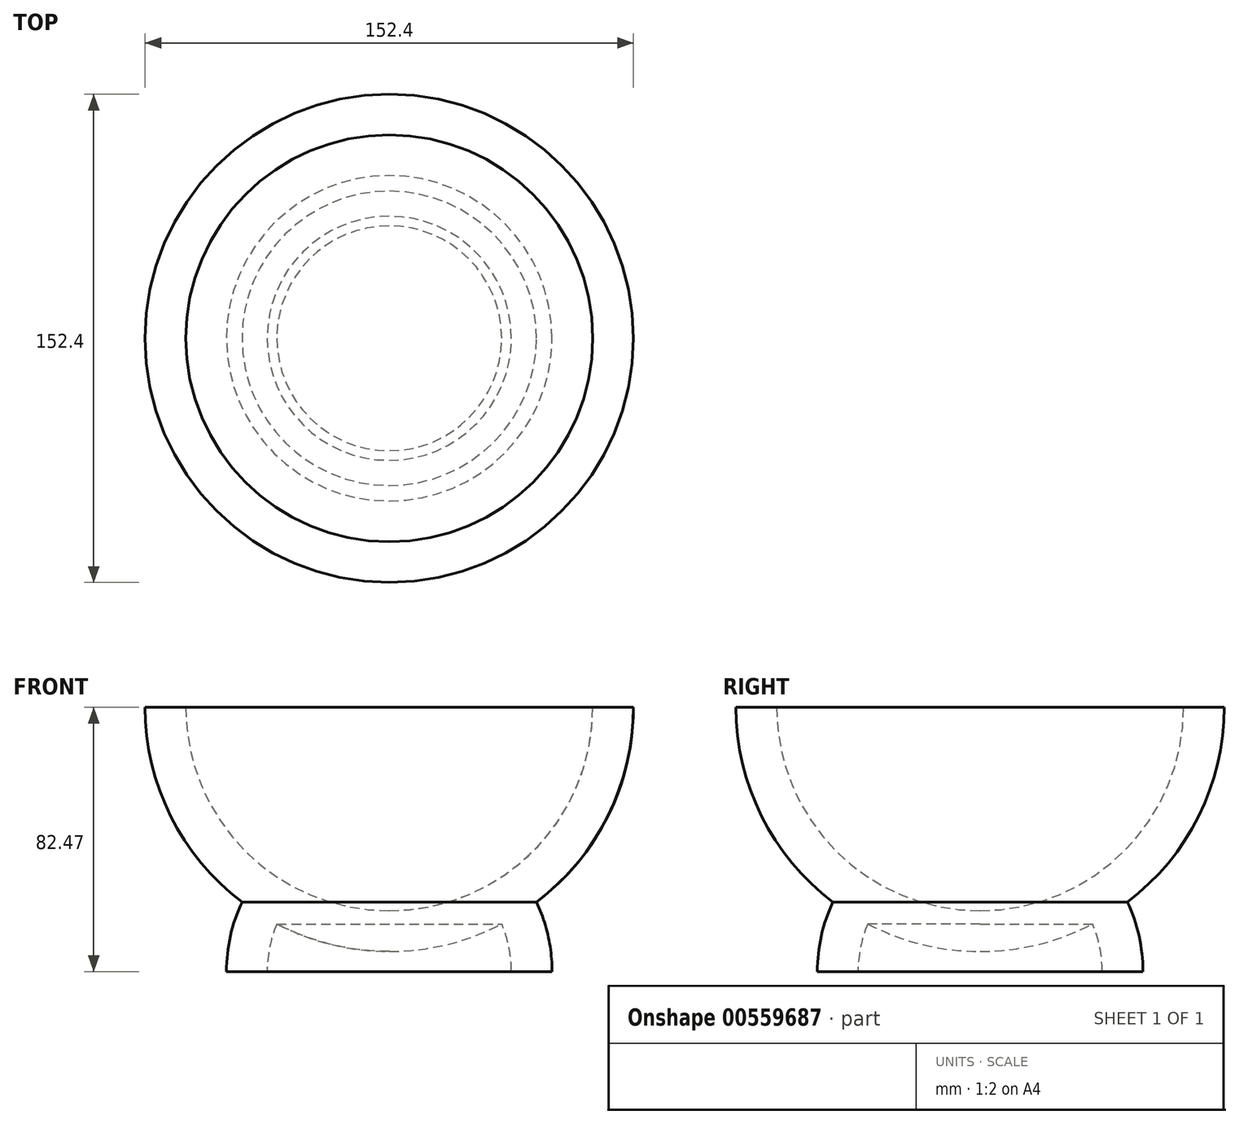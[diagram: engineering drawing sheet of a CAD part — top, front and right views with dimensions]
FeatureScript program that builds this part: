
annotation { "Feature Type Name" : "Feature", "Feature Type Description" : "" }
export const myFeature = defineFeature(function(context is Context, id is Id, definition is map)
    precondition{}
    {
        {
            var Q0;
            Q0=qCreatedBy(makeId("Front.planeOp"),FACE);
            var sketch = newSketch(context, id + "F0", { "sketchPlane" : qUnion([Q0])});
            skLineSegment(sketch, "E0", {"start": v(0, 76.47) * mm, "end": v(0, -73.73) * mm, "construction": true});
            skSolve(sketch);
        }
        {
            var Q0;
            Q0=qCreatedBy(makeId("Front.planeOp"),FACE);
            var sketch = newSketch(context, id + "F1", { "sketchPlane" : qUnion([Q0])});
            skArc(sketch, "E1", {"start": v(25.4, -41.23) * mm, "mid": v(24.79, -35.68) * mm, "end": v(22.97, -30.4) * mm});
            skArc(sketch, "E2", {"start": v(19.05, -41.23) * mm, "mid": v(18.67, -37.45) * mm, "end": v(17.55, -33.82) * mm});
            skLineSegment(sketch, "E3", {"start": v(0, 0) * mm, "end": v(0, -73.77) * mm});
            skLineSegment(sketch, "E4.trimOffspring", {"start": v(31.75, 0) * mm, "end": v(38.1, 0) * mm});
            skArc(sketch, "E5.trimOffspring", {"start": v(0, -31.75) * mm, "mid": v(22.45, -22.45) * mm, "end": v(31.75, 0) * mm});
            skArc(sketch, "E6.trimOffspring", {"start": v(0, -38.1) * mm, "mid": v(9.03, -37.01) * mm, "end": v(17.55, -33.82) * mm});
            skLineSegment(sketch, "E7.trimOffspring", {"start": v(19.05, -41.23) * mm, "end": v(25.4, -41.23) * mm});
            skArc(sketch, "E8.trimOffspring", {"start": v(22.97, -30.4) * mm, "mid": v(34.1, -16.98) * mm, "end": v(38.1, 0) * mm});
            skSolve(sketch);
        }
        {
            var Q0;
            Q0=makeQuery(id+"F1.imprint","IMPRINT",FACE,{"disambiguationData":[TD([[makeQuery(id+"F1.imprint","IMPRINT",EDGE,{"derivedFrom":sQuery(id+"F1.wireOp",EDGE,"E1")}),1.0]])]});
            var Q1;
            Q1=sQuery(id+"F0.wireOp",EDGE,"E0");
            revolve(context, id + "F2", {"entities" : qUnion([Q0]), "axis" : qUnion([Q1]), "revolveType" : RevolveType.FULL});
        }
        {
            var Q0;
            Q0=makeQuery(id+"F2.opRevolve","SWEPT_BODY",BODY,{"disambiguationData":[OSD([sQuery(id+"F1.wireOp",EDGE,"E1"),sQuery(id+"F1.wireOp",EDGE,"E2"),sQuery(id+"F1.wireOp",EDGE,"E3"),sQuery(id+"F1.wireOp",EDGE,"E4.trimOffspring"),sQuery(id+"F1.wireOp",EDGE,"E5.trimOffspring"),sQuery(id+"F1.wireOp",EDGE,"E6.trimOffspring"),sQuery(id+"F1.wireOp",EDGE,"E7.trimOffspring"),sQuery(id+"F1.wireOp",EDGE,"E8.trimOffspring")])]});
            var Q1;
            Q1=qCreatedBy(makeId("Origin.pointOp"),VERTEX);
            transform(context, id + "F3", {"entities" : qUnion([Q0]), "transformType" : TransformType.SCALE_UNIFORMLY, "scale" : 2, "scalePoint" : qUnion([Q1]), "makeCopy" : false});
        }
    });
